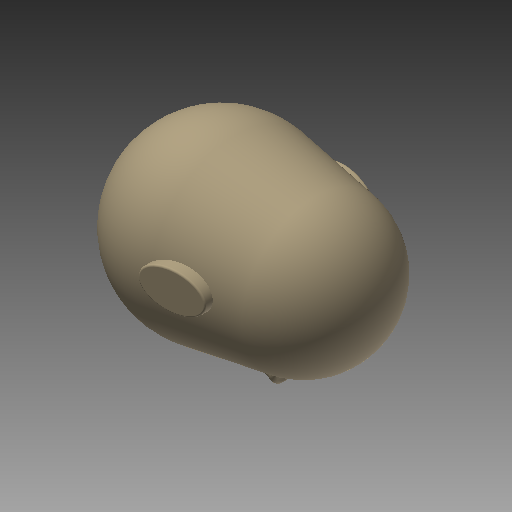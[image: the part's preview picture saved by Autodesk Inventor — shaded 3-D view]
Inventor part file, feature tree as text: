
AUTODESK INVENTOR PART (.ipt)
format: ipt  version: 2022 (Build 260153000, 153)  size: 293,376 bytes
history: native  units: mm (DEFAULTED — no unit token found)
features: sketch x5, extrude x3, revolve x2, fillet x2, other x1, mirror x1, projected_geometry x1
ambient origin geometry x8: Origin, YZ Plane, XZ Plane, XY Plane, X Axis, Y Axis, Z Axis, Center Point
bodies: Solid1 (feature_tree)
feature tree (15):
  other  "iMan - 2D BODY"
  revolve  "Revolution1"  [1 undecoded]
  extrude  "Extrusion1"  Depth=164.868408mm
  extrude  "Extrusion2"  Depth=26.547202mm
  mirror  "Mirror1"
  fillet  "Fillet1"  Radius=20.905922mm
  revolve  "Revolution2"  [1 undecoded]
  extrude  "Extrusion3"  Depth=3.879257mm
  fillet  "Fillet2"  [1 undecoded]
  sketch  "Sketch2"  dims[d1=10.0mm d25=269.13586mm]
  sketch  "Sketch3"  dims[d26=193.962833mm d27=164.868408mm]
  projected_geometry  "Projected Loop1"
  sketch  "Sketch4"  dims[d28=90.0deg d29=26.547202mm d30=20.905922mm]
  sketch  "Sketch5"  dims[d31=33.184003mm d32=203.660974mm]
  sketch  "Sketch6"  dims[d33=0.0mm d34=203.660974mm d35=0.0mm d36=1.939628mm d37=30.0deg d38=180.0deg d39=203.660974mm d40=0.0mm d41=3.879257mm d42=53.827172mm d43=8.89mm]
note: 3 required parameter values undecoded (feature->parameter linkage not recoverable at this tier; creation-order binding heuristic only, values carry confidence <= 0.55)